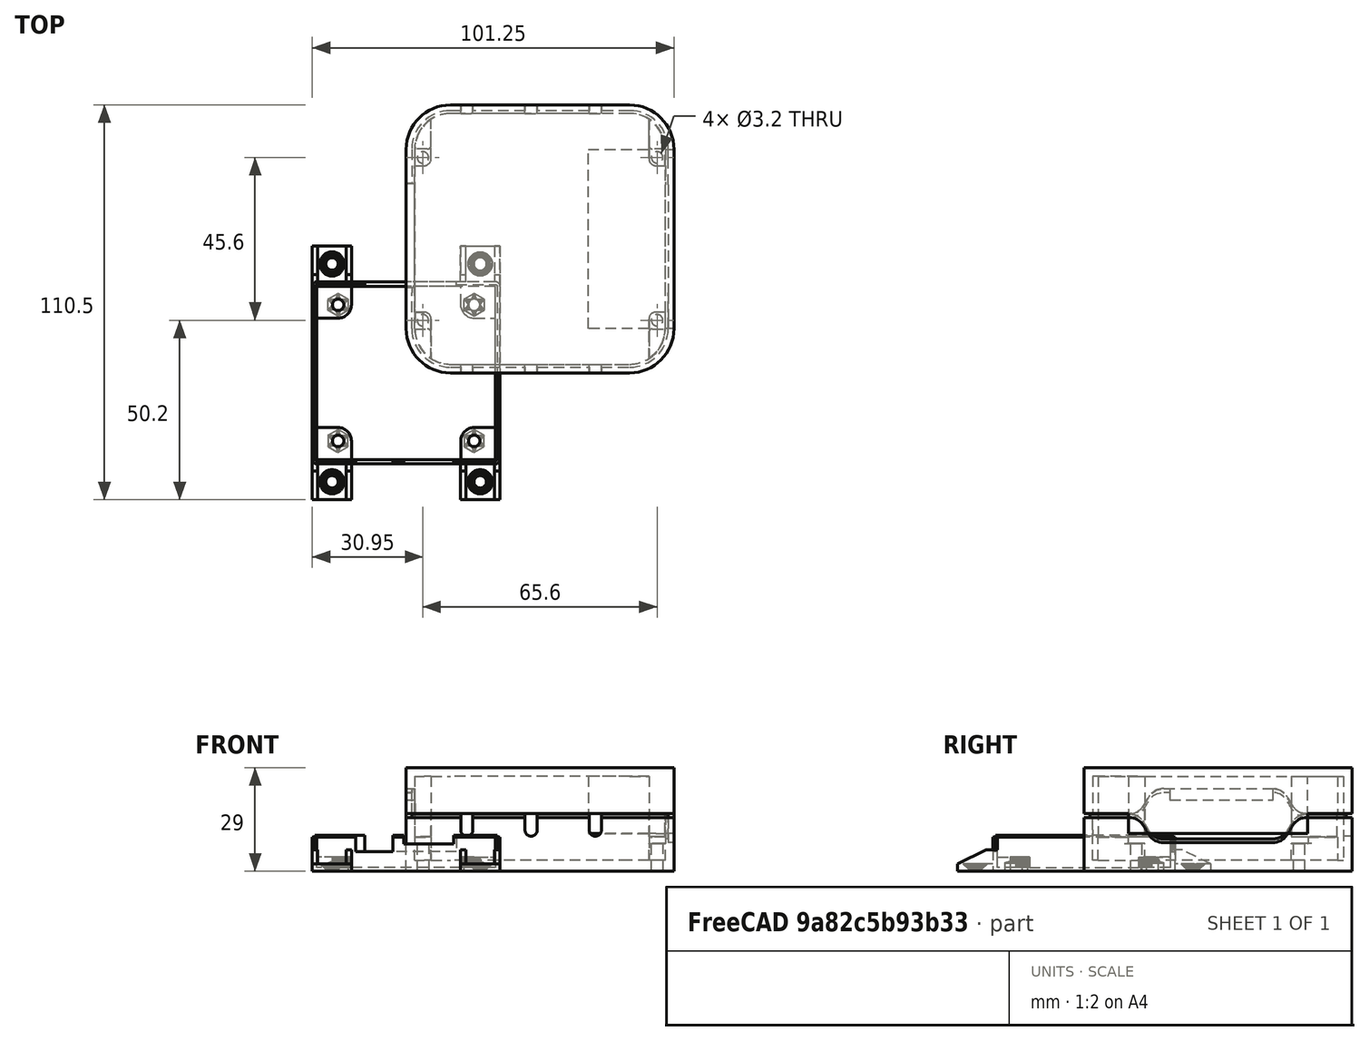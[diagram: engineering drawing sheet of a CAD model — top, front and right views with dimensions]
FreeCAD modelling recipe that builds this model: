
FCSTD DOCUMENT  (FreeCAD 1.0R39109 (Git))
Label: peepSensorCenter
License: All rights reserved
LicenseURL: https://en.wikipedia.org/wiki/All_rights_reserved
objects: Sketcher::SketchObject×20, PartDesign::Pocket×11, PartDesign::Pad×9, PartDesign::Fillet×5, Part::Feature×2, PartDesign::Body×2, Mesh::Feature×1, Part::Refine×1, PartDesign::Thickness×1
note: 123 computed .brp shape members not serialized (recipe doc carries the construction recipe); baked Part::Feature solids carry a one-line shape summary decoded from their .brp

FEATURE [Sketcher::SketchObject] Sketch  label="BaseBrickSketch"
  ArcFitTolerance = 1e-06
  AttachmentSupport = -> [XY_Plane]
  FullyConstrained = true
  MakeInternals = false
  MapMode = 5
  sketch-geometry (4):
    g0: LineSegment StartX=0 StartY=0 StartZ=0 EndX=75 EndY=0 EndZ=0
    g1: LineSegment StartX=75 StartY=0 StartZ=0 EndX=75 EndY=75 EndZ=0
    g2: LineSegment StartX=75 StartY=75 StartZ=0 EndX=0 EndY=75 EndZ=0
    g3: LineSegment StartX=0 StartY=75 StartZ=0 EndX=0 EndY=0 EndZ=0
  constraints (11):
    c: Coincident(g0,g1)
    c: Coincident(g1,g2)
    c: Coincident(g2,g3)
    c: Coincident(g3,g0)
    c: Horizontal(g0)
    c: Horizontal(g2)
    c: Vertical(g1)
    c: Vertical(g3)
    c: Coincident(g0,g-1)
    c: DistanceY(g3,g3) = 75
    c: DistanceX(g2,g2) = 75
FEATURE [PartDesign::Pad] Pad  label="BaseBrick"
  Direction = (0,0,1)
  Length = 15
  Length2 = 10
  Profile = -> Sketch
  ReferenceAxis = -> Sketch [N_Axis]
  Refine = true
  Suppressed = false
  Type = 0
FEATURE [Sketcher::SketchObject] Sketch001  label="BrickHoleSketch"
  ArcFitTolerance = 1e-06
  AttachmentSupport = -> [Pad]
  ExternalGeometry = -> [Pad]
  FullyConstrained = true
  MakeInternals = false
  MapMode = 5
  Placement = pos=(0,0,15) rot=(0,0,1;0rad)
  sketch-geometry (4):
    g0: LineSegment StartX=2.4 StartY=72.6 StartZ=0 EndX=2.4 EndY=2.4 EndZ=0
    g1: LineSegment StartX=2.4 StartY=2.4 StartZ=0 EndX=72.6 EndY=2.4 EndZ=0
    g2: LineSegment StartX=72.6 StartY=2.4 StartZ=0 EndX=72.6 EndY=72.6 EndZ=0
    g3: LineSegment StartX=72.6 StartY=72.6 StartZ=0 EndX=2.4 EndY=72.6 EndZ=0
  constraints (12):
    c: Coincident(g0,g1)
    c: Coincident(g1,g2)
    c: Coincident(g2,g3)
    c: Coincident(g3,g0)
    c: Vertical(g0)
    c: Vertical(g2)
    c: Horizontal(g1)
    c: Horizontal(g3)
    c: DistanceY(g0,g-4) = 2.4
    c: DistanceX(g-4,g0) = 2.4
    c: DistanceY(g-6,g1) = 2.4
    c: DistanceX(g1,g-6) = 2.4
FEATURE [PartDesign::Pocket] Pocket  label="BrickHole"
  BaseFeature = -> Pad
  Direction = (0,0,-1)
  Length = 12
  Length2 = 5
  Profile = -> Sketch001
  ReferenceAxis = -> Sketch001 [N_Axis]
  Refine = true
  Suppressed = false
  Type = 0
  expr: Length = 15 - 3
FEATURE [Sketcher::SketchObject] Sketch002  label="PCBBaseSketch"
  ArcFitTolerance = 1e-06
  AttachmentSupport = -> [Pocket]
  ExternalGeometry = -> [Pocket]
  FullyConstrained = true
  MakeInternals = false
  MapMode = 5
  Placement = pos=(0,0,3) rot=(0,0,1;0rad)
  sketch-geometry (21):
    g0: LineSegment [constr] StartX=2.4 StartY=62.6 StartZ=0 EndX=2.4 EndY=12.4 EndZ=0
    g1: LineSegment [constr] StartX=2.4 StartY=12.4 StartZ=0 EndX=72.6 EndY=12.4 EndZ=0
    g2: LineSegment [constr] StartX=72.6 StartY=12.4 StartZ=0 EndX=72.6 EndY=62.6 EndZ=0
    g3: LineSegment [constr] StartX=72.6 StartY=62.6 StartZ=0 EndX=2.4 EndY=62.6 EndZ=0
    g4: GeomPoint X=2.4 Y=37.5 Z=0
    g5: LineSegment StartX=2.4 StartY=62.6 StartZ=0 EndX=2.4 EndY=58 EndZ=0
    g6: LineSegment StartX=2.4 StartY=58 StartZ=0 EndX=7 EndY=58 EndZ=0
    g7: LineSegment StartX=7 StartY=58 StartZ=0 EndX=7 EndY=62.6 EndZ=0
    g8: LineSegment StartX=7 StartY=62.6 StartZ=0 EndX=2.4 EndY=62.6 EndZ=0
    g9: LineSegment StartX=72.6 StartY=62.6 StartZ=0 EndX=68 EndY=62.6 EndZ=0
    g10: LineSegment StartX=68 StartY=62.6 StartZ=0 EndX=68 EndY=58 EndZ=0
    g11: LineSegment StartX=68 StartY=58 StartZ=0 EndX=72.6 EndY=58 EndZ=0
    g12: LineSegment StartX=72.6 StartY=58 StartZ=0 EndX=72.6 EndY=62.6 EndZ=0
    g13: LineSegment StartX=72.6 StartY=12.4 StartZ=0 EndX=72.6 EndY=17 EndZ=0
    g14: LineSegment StartX=72.6 StartY=17 StartZ=0 EndX=68 EndY=17 EndZ=0
    g15: LineSegment StartX=68 StartY=17 StartZ=0 EndX=68 EndY=12.4 EndZ=0
    g16: LineSegment StartX=68 StartY=12.4 StartZ=0 EndX=72.6 EndY=12.4 EndZ=0
    g17: LineSegment StartX=2.4 StartY=12.4 StartZ=0 EndX=7 EndY=12.4 EndZ=0
    g18: LineSegment StartX=7 StartY=12.4 StartZ=0 EndX=7 EndY=17 EndZ=0
    g19: LineSegment StartX=7 StartY=17 StartZ=0 EndX=2.4 EndY=17 EndZ=0
    g20: LineSegment StartX=2.4 StartY=17 StartZ=0 EndX=2.4 EndY=12.4 EndZ=0
  constraints (56):
    c: Coincident(g0,g1)
    c: Coincident(g1,g2)
    c: Coincident(g2,g3)
    c: Coincident(g3,g0)
    c: Vertical(g0)
    c: Vertical(g2)
    c: Horizontal(g1)
    c: Horizontal(g3)
    c: Symmetric(g-3,g-3,g4)
    c: Symmetric(g0,g0,g4)
    c: Coincident(g5,g6)
    c: Coincident(g6,g7)
    c: Coincident(g7,g8)
    c: Coincident(g8,g5)
    c: Vertical(g5)
    c: Vertical(g7)
    c: Horizontal(g6)
    c: Horizontal(g8)
    c: Coincident(g5,g0)
    c: Coincident(g9,g10)
    c: Coincident(g10,g11)
    c: Coincident(g11,g12)
    c: Coincident(g12,g9)
    c: Horizontal(g9)
    c: Horizontal(g11)
    c: Vertical(g10)
    c: Vertical(g12)
    c: Coincident(g9,g2)
    c: Coincident(g13,g14)
    c: Coincident(g14,g15)
    c: Coincident(g15,g16)
    c: Coincident(g16,g13)
    c: Vertical(g13)
    c: Vertical(g15)
    c: Horizontal(g14)
    c: Horizontal(g16)
    c: Coincident(g13,g1)
    c: Coincident(g17,g18)
    c: Coincident(g18,g19)
    c: Coincident(g19,g20)
    c: Coincident(g20,g17)
    c: Horizontal(g17)
    c: Horizontal(g19)
    c: Vertical(g18)
    c: Vertical(g20)
    c: Coincident(g17,g0)
    c: DistanceX(g19,g19) = 4.6
    c: DistanceX(g6,g6) = 4.6
    c: DistanceX(g11,g11) = 4.6
    c: DistanceX(g14,g14) = 4.6
    c: DistanceY(g15,g15) = 4.6
    c: DistanceY(g10,g10) = 4.6
    c: DistanceY(g7,g7) = 4.6
    c: DistanceY(g18,g18) = 4.6
    c: PointOnObject(g1,g-7)
    c: DistanceY(g1,g2) = 50.2
FEATURE [PartDesign::Pad] Pad001  label="PCBBase"
  BaseFeature = -> Pocket
  Direction = (0,0,1)
  Length = 4.8
  Length2 = 10
  Profile = -> Sketch002
  ReferenceAxis = -> Sketch002 [N_Axis]
  Refine = true
  Suppressed = false
  Type = 0
FEATURE [Mesh::Feature] bottom
FEATURE [Part::Feature] bottom001
  shape: bbox 52.5 x 71 x 10 mm, 3748 faces, 0 solids (baked)
FEATURE [Part::Feature] bottom001_solid  label="bottom001 (Solid)"
  shape: bbox 52.5 x 71 x 10 mm, 3748 faces (baked)
FEATURE [Part::Refine] bottom001_solid001  label="bottom001 (Solid)001"
  Source = -> bottom001_solid
FEATURE [Sketcher::SketchObject] Sketch003  label="ScrewHoleSketch"
  ArcFitTolerance = 1e-06
  AttachmentSupport = -> [Pad001]
  ExternalGeometry = -> [Pad001]
  FullyConstrained = true
  MakeInternals = false
  MapMode = 5
  Placement = pos=(0,0,7.8) rot=(0,0,1;0rad)
  sketch-geometry (20):
    g0: LineSegment [constr] StartX=7 StartY=60.3 StartZ=0 EndX=4.7 EndY=60.3 EndZ=0
    g1: LineSegment [constr] StartX=4.7 StartY=60.3 StartZ=0 EndX=4.7 EndY=58 EndZ=0
    g2: LineSegment [constr] StartX=4.7 StartY=58 StartZ=0 EndX=7 EndY=58 EndZ=0
    g3: LineSegment [constr] StartX=7 StartY=58 StartZ=0 EndX=7 EndY=60.3 EndZ=0
    g4: LineSegment [constr] StartX=4.7 StartY=17 StartZ=0 EndX=4.7 EndY=14.7 EndZ=0
    g5: LineSegment [constr] StartX=4.7 StartY=14.7 StartZ=0 EndX=7 EndY=14.7 EndZ=0
    g6: LineSegment [constr] StartX=7 StartY=14.7 StartZ=0 EndX=7 EndY=17 EndZ=0
    g7: LineSegment [constr] StartX=7 StartY=17 StartZ=0 EndX=4.7 EndY=17 EndZ=0
    g8: LineSegment [constr] StartX=70.3 StartY=17 StartZ=0 EndX=68 EndY=17 EndZ=0
    g9: LineSegment [constr] StartX=68 StartY=17 StartZ=0 EndX=68 EndY=14.7 EndZ=0
    g10: LineSegment [constr] StartX=68 StartY=14.7 StartZ=0 EndX=70.3 EndY=14.7 EndZ=0
    g11: LineSegment [constr] StartX=70.3 StartY=14.7 StartZ=0 EndX=70.3 EndY=17 EndZ=0
    g12: LineSegment [constr] StartX=68 StartY=60.3 StartZ=0 EndX=68 EndY=58 EndZ=0
    g13: LineSegment [constr] StartX=68 StartY=58 StartZ=0 EndX=70.3 EndY=58 EndZ=0
    g14: LineSegment [constr] StartX=70.3 StartY=58 StartZ=0 EndX=70.3 EndY=60.3 EndZ=0
    g15: LineSegment [constr] StartX=70.3 StartY=60.3 StartZ=0 EndX=68 EndY=60.3 EndZ=0
    g16: Circle CenterX=4.7 CenterY=60.3 CenterZ=0 NormalX=0 NormalY=0 NormalZ=1 AngleXU=0 Radius=1.6
    g17: Circle CenterX=4.7 CenterY=14.7 CenterZ=0 NormalX=0 NormalY=0 NormalZ=1 AngleXU=0 Radius=1.6
    g18: Circle CenterX=70.3 CenterY=14.7 CenterZ=0 NormalX=0 NormalY=0 NormalZ=1 AngleXU=0 Radius=1.6
    g19: Circle CenterX=70.3 CenterY=60.3 CenterZ=0 NormalX=0 NormalY=0 NormalZ=1 AngleXU=0 Radius=1.6
  constraints (48):
    c: Coincident(g0,g1)
    c: Coincident(g1,g2)
    c: Coincident(g2,g3)
    c: Coincident(g3,g0)
    c: Horizontal(g0)
    c: Horizontal(g2)
    c: Vertical(g1)
    c: Vertical(g3)
    c: Symmetric(g-3,g-3,g0)
    c: Symmetric(g-4,g-4,g1)
    c: Coincident(g4,g5)
    c: Coincident(g5,g6)
    c: Coincident(g6,g7)
    c: Coincident(g7,g4)
    c: Vertical(g4)
    c: Vertical(g6)
    c: Horizontal(g5)
    c: Horizontal(g7)
    c: Symmetric(g-5,g-5,g4)
    c: Symmetric(g-6,g-6,g5)
    c: Coincident(g8,g9)
    c: Coincident(g9,g10)
    c: Coincident(g10,g11)
    c: Coincident(g11,g8)
    c: Horizontal(g8)
    c: Horizontal(g10)
    c: Vertical(g9)
    c: Vertical(g11)
    c: Symmetric(g-8,g-8,g8)
    c: Symmetric(g-7,g-7,g9)
    c: Coincident(g12,g13)
    c: Coincident(g13,g14)
    c: Coincident(g14,g15)
    c: Coincident(g15,g12)
    c: Vertical(g12)
    c: Vertical(g14)
    c: Horizontal(g13)
    c: Horizontal(g15)
    c: Symmetric(g-9,g-9,g12)
    c: Symmetric(g-10,g-10,g13)
    c: Coincident(g16,g0)
    c: Coincident(g17,g4)
    c: Coincident(g18,g10)
    c: Coincident(g19,g14)
    c: Diameter(g19) = 3.2
    c: Diameter(g18) = 3.2
    c: Diameter(g17) = 3.2
    c: Diameter(g16) = 3.2
FEATURE [PartDesign::Pocket] Pocket001  label="ScrewHole"
  BaseFeature = -> Pad001
  Direction = (0,0,-1)
  Length = 5
  Length2 = 5
  Profile = -> Sketch003
  ReferenceAxis = -> Sketch003 [N_Axis]
  Refine = true
  Suppressed = false
  Type = 1
FEATURE [Sketcher::SketchObject] Sketch004  label="PCBStopSketch"
  ArcFitTolerance = 1e-06
  AttachmentSupport = -> [Pocket001]
  ExternalGeometry = -> [Pocket001]
  FullyConstrained = true
  MakeInternals = false
  MapMode = 5
  Placement = pos=(0,0,3) rot=(0,0,1;0rad)
  sketch-geometry (16):
    g0: LineSegment StartX=68 StartY=12.4 StartZ=0 EndX=68 EndY=2.4 EndZ=0
    g1: LineSegment StartX=68 StartY=2.4 StartZ=0 EndX=72.6 EndY=2.4 EndZ=0
    g2: LineSegment StartX=72.6 StartY=2.4 StartZ=0 EndX=72.6 EndY=12.4 EndZ=0
    g3: LineSegment StartX=72.6 StartY=12.4 StartZ=0 EndX=68 EndY=12.4 EndZ=0
    g4: LineSegment StartX=68 StartY=62.6 StartZ=0 EndX=72.6 EndY=62.6 EndZ=0
    g5: LineSegment StartX=72.6 StartY=62.6 StartZ=0 EndX=72.6 EndY=72.6 EndZ=0
    g6: LineSegment StartX=72.6 StartY=72.6 StartZ=0 EndX=68 EndY=72.6 EndZ=0
    g7: LineSegment StartX=68 StartY=72.6 StartZ=0 EndX=68 EndY=62.6 EndZ=0
    g8: LineSegment StartX=7 StartY=62.6 StartZ=0 EndX=7 EndY=72.6 EndZ=0
    g9: LineSegment StartX=7 StartY=72.6 StartZ=0 EndX=2.4 EndY=72.6 EndZ=0
    g10: LineSegment StartX=2.4 StartY=72.6 StartZ=0 EndX=2.4 EndY=62.6 EndZ=0
    g11: LineSegment StartX=2.4 StartY=62.6 StartZ=0 EndX=7 EndY=62.6 EndZ=0
    g12: LineSegment StartX=7 StartY=12.4 StartZ=0 EndX=2.4 EndY=12.4 EndZ=0
    g13: LineSegment StartX=2.4 StartY=12.4 StartZ=0 EndX=2.4 EndY=2.4 EndZ=0
    g14: LineSegment StartX=2.4 StartY=2.4 StartZ=0 EndX=7 EndY=2.4 EndZ=0
    g15: LineSegment StartX=7 StartY=2.4 StartZ=0 EndX=7 EndY=12.4 EndZ=0
  constraints (40):
    c: Coincident(g0,g1)
    c: Coincident(g1,g2)
    c: Coincident(g2,g3)
    c: Coincident(g3,g0)
    c: Vertical(g0)
    c: Vertical(g2)
    c: Horizontal(g1)
    c: Horizontal(g3)
    c: Coincident(g0,g-11)
    c: Coincident(g1,g-12)
    c: Coincident(g4,g5)
    c: Coincident(g5,g6)
    c: Coincident(g6,g7)
    c: Coincident(g7,g4)
    c: Horizontal(g4)
    c: Horizontal(g6)
    c: Vertical(g5)
    c: Vertical(g7)
    c: Coincident(g4,g-6)
    c: Coincident(g5,g-7)
    c: Coincident(g8,g9)
    c: Coincident(g9,g10)
    c: Coincident(g10,g11)
    c: Coincident(g11,g8)
    c: Vertical(g8)
    c: Vertical(g10)
    c: Horizontal(g9)
    c: Horizontal(g11)
    c: Coincident(g8,g-5)
    c: Coincident(g9,g-4)
    c: Coincident(g12,g13)
    c: Coincident(g13,g14)
    c: Coincident(g14,g15)
    c: Coincident(g15,g12)
    c: Horizontal(g12)
    c: Horizontal(g14)
    c: Vertical(g13)
    c: Vertical(g15)
    c: Coincident(g12,g-10)
    c: Coincident(g13,g-9)
FEATURE [PartDesign::Pad] Pad002  label="PCBStop"
  BaseFeature = -> Pocket001
  Direction = (0,0,1)
  Length = 6.5
  Length2 = 10
  Profile = -> Sketch004
  ReferenceAxis = -> Sketch004 [N_Axis]
  Refine = true
  Suppressed = false
  Type = 0
FEATURE [PartDesign::Fillet] Fillet  label="InnerFillet"
  Base = -> Pad002 [Edge39,Edge46,Edge40,Edge29]
  BaseFeature = -> Pad002
  Radius = 10
  Refine = true
  SupportTransform = false
  Suppressed = false
  UseAllEdges = false
FEATURE [PartDesign::Fillet] Fillet001  label="OuterFillet"
  Base = -> Fillet [Edge50,Edge52,Edge49,Edge54]
  BaseFeature = -> Fillet
  Radius = 12.4
  Refine = true
  SupportTransform = false
  Suppressed = false
  UseAllEdges = false
FEATURE [Sketcher::SketchObject] Sketch005  label="InterlaceWallSketch"
  ArcFitTolerance = 1e-06
  AttachmentSupport = -> [Fillet001]
  ExternalGeometry = -> [Fillet001]
  FullyConstrained = true
  MakeInternals = false
  MapMode = 5
  Placement = pos=(0,0,15) rot=(0,0,1;0rad)
  sketch-geometry (20):
    g0: LineSegment StartX=1.6 StartY=62.6 StartZ=0 EndX=1.6 EndY=12.4 EndZ=0
    g1: LineSegment StartX=12.4 StartY=1.6 StartZ=0 EndX=62.6 EndY=1.6 EndZ=0
    g2: LineSegment StartX=73.4 StartY=12.4 StartZ=0 EndX=73.4 EndY=62.6 EndZ=0
    g3: LineSegment StartX=62.6 StartY=73.4 StartZ=0 EndX=12.4 EndY=73.4 EndZ=0
    g4: ArcOfCircle CenterX=12.4 CenterY=62.6 CenterZ=0 NormalX=0 NormalY=0 NormalZ=1 AngleXU=0 Radius=10.8 StartAngle=1.5708 EndAngle=3.14159
    g5: ArcOfCircle CenterX=12.4 CenterY=12.4 CenterZ=0 NormalX=0 NormalY=0 NormalZ=1 AngleXU=0 Radius=10.8 StartAngle=3.14159 EndAngle=4.71239
    g6: ArcOfCircle CenterX=62.6 CenterY=12.4 CenterZ=0 NormalX=0 NormalY=0 NormalZ=1 AngleXU=0 Radius=10.8 StartAngle=4.71239 EndAngle=6.28319
    g7: ArcOfCircle CenterX=62.6 CenterY=62.6 CenterZ=0 NormalX=0 NormalY=0 NormalZ=1 AngleXU=0 Radius=10.8 StartAngle=0 EndAngle=1.5708
    g8: GeomPoint [constr] X=1.6 Y=73.4 Z=0
    g9: GeomPoint [constr] X=73.4 Y=1.6 Z=0
    g10: LineSegment StartX=2.4 StartY=62.6 StartZ=0 EndX=2.4 EndY=12.4 EndZ=0
    g11: LineSegment StartX=12.4 StartY=2.4 StartZ=0 EndX=62.6 EndY=2.4 EndZ=0
    g12: LineSegment StartX=72.6 StartY=12.4 StartZ=0 EndX=72.6 EndY=62.6 EndZ=0
    g13: LineSegment StartX=62.6 StartY=72.6 StartZ=0 EndX=12.4 EndY=72.6 EndZ=0
    g14: ArcOfCircle CenterX=12.4 CenterY=62.6 CenterZ=0 NormalX=0 NormalY=0 NormalZ=1 AngleXU=0 Radius=10 StartAngle=1.5708 EndAngle=3.14159
    g15: ArcOfCircle CenterX=12.4 CenterY=12.4 CenterZ=0 NormalX=0 NormalY=0 NormalZ=1 AngleXU=0 Radius=10 StartAngle=3.14159 EndAngle=4.71239
    g16: ArcOfCircle CenterX=62.6 CenterY=12.4 CenterZ=0 NormalX=0 NormalY=0 NormalZ=1 AngleXU=0 Radius=10 StartAngle=4.71239 EndAngle=6.28319
    g17: ArcOfCircle CenterX=62.6 CenterY=62.6 CenterZ=0 NormalX=0 NormalY=0 NormalZ=1 AngleXU=0 Radius=10 StartAngle=1e-16 EndAngle=1.5708
    g18: GeomPoint [constr] X=2.4 Y=72.6 Z=0
    g19: GeomPoint [constr] X=72.6 Y=2.4 Z=0
  constraints (45):
    c: Tangent(g0,g4) = -1.5708
    c: Tangent(g0,g5) = -1.5708
    c: Tangent(g1,g5) = -1.5708
    c: Tangent(g1,g6) = -1.5708
    c: Tangent(g2,g6) = -1.5708
    c: Tangent(g2,g7) = -1.5708
    c: Tangent(g3,g7) = -1.5708
    c: Tangent(g3,g4) = -1.5708
    c: Vertical(g0)
    c: Vertical(g2)
    c: Horizontal(g1)
    c: Horizontal(g3)
    c: Equal(g4,g5)
    c: Equal(g5,g6)
    c: Equal(g6,g7)
    c: PointOnObject(g8,g0)
    c: PointOnObject(g8,g3)
    c: PointOnObject(g9,g1)
    c: PointOnObject(g9,g2)
    c: Vertical(g3,g-3)
    c: Horizontal(g0,g-4)
    c: Horizontal(g2,g-5)
    c: DistanceX(g0,g-4) = 0.8
    c: Vertical(g1,g-6)
    c: Tangent(g10,g14) = -1.5708
    c: Tangent(g10,g15) = -1.5708
    c: Tangent(g11,g15) = -1.5708
    c: Tangent(g11,g16) = -1.5708
    c: Tangent(g12,g16) = -1.5708
    c: Tangent(g12,g17) = -1.5708
    c: Tangent(g13,g17) = -1.5708
    c: Tangent(g13,g14) = -1.5708
    c: Vertical(g10)
    c: Vertical(g12)
    c: Horizontal(g13)
    c: Equal(g14,g15)
    c: Equal(g15,g16)
    c: Equal(g16,g17)
    c: PointOnObject(g18,g10)
    c: PointOnObject(g18,g13)
    c: PointOnObject(g19,g11)
    c: PointOnObject(g19,g12)
    c: Coincident(g12,g-5)
    c: Coincident(g11,g-6)
    c: Coincident(g10,g-4)
FEATURE [PartDesign::Pad] Pad003  label="InterlaceWall"
  BaseFeature = -> Fillet001
  Direction = (0,0,1)
  Length = 1
  Length2 = 10
  Profile = -> Sketch005
  ReferenceAxis = -> Sketch005 [N_Axis]
  Refine = true
  Suppressed = false
  Type = 0
FEATURE [Sketcher::SketchObject] Sketch006  label="WireHolesSketch"
  ArcFitTolerance = 1e-06
  AttachmentSupport = -> [XZ_Plane]
  ExternalGeometry = -> [Pad003]
  FullyConstrained = true
  MakeInternals = false
  MapMode = 5
  Placement = pos=(0,0,0) rot=(1,0,0;1.5708rad)
  sketch-geometry (13):
    g0: ArcOfCircle CenterX=17 CenterY=16 CenterZ=0 NormalX=0 NormalY=0 NormalZ=1 AngleXU=0 Radius=1.7 StartAngle=9e-16 EndAngle=3.14159
    g1: ArcOfCircle CenterX=17 CenterY=11.5 CenterZ=0 NormalX=0 NormalY=0 NormalZ=1 AngleXU=0 Radius=1.7 StartAngle=3.14159 EndAngle=6.28319
    g2: LineSegment StartX=18.7 StartY=16 StartZ=0 EndX=18.7 EndY=11.5 EndZ=0
    g3: LineSegment StartX=15.3 StartY=16 StartZ=0 EndX=15.3 EndY=11.5 EndZ=0
    g4: GeomPoint [constr] X=7 Y=11.5 Z=0
    g5: ArcOfCircle CenterX=35 CenterY=16 CenterZ=0 NormalX=0 NormalY=0 NormalZ=1 AngleXU=0 Radius=1.7 StartAngle=3.74e-14 EndAngle=3.14159
    g6: ArcOfCircle CenterX=35 CenterY=11.5 CenterZ=0 NormalX=0 NormalY=0 NormalZ=1 AngleXU=0 Radius=1.7 StartAngle=3.14159 EndAngle=6.28319
    g7: LineSegment StartX=36.7 StartY=16 StartZ=0 EndX=36.7 EndY=11.5 EndZ=0
    g8: LineSegment StartX=33.3 StartY=16 StartZ=0 EndX=33.3 EndY=11.5 EndZ=0
    g9: ArcOfCircle CenterX=53 CenterY=16 CenterZ=0 NormalX=0 NormalY=0 NormalZ=1 AngleXU=0 Radius=1.7 StartAngle=4e-16 EndAngle=3.14159
    g10: ArcOfCircle CenterX=53 CenterY=11.5 CenterZ=0 NormalX=0 NormalY=0 NormalZ=1 AngleXU=0 Radius=1.7 StartAngle=3.14159 EndAngle=6.28319
    g11: LineSegment StartX=54.7 StartY=16 StartZ=0 EndX=54.7 EndY=11.5 EndZ=0
    g12: LineSegment StartX=51.3 StartY=16 StartZ=0 EndX=51.3 EndY=11.5 EndZ=0
  constraints (32):
    c: Tangent(g0,g2) = 1.5708
    c: Tangent(g0,g3) = -1.5708
    c: Tangent(g1,g2) = 1.5708
    c: Tangent(g1,g3) = -1.5708
    c: Equal(g0,g1)
    c: PointOnObject(g0,g-3)
    c: Vertical(g2)
    c: DistanceX(g1,g1) = 3.4
    c: DistanceY(g-5,g4) = 2
    c: Horizontal(g4,g1)
    c: Vertical(g-5,g4)
    c: DistanceX(g4,g1) = 10
    c: Tangent(g5,g7) = 1.5708
    c: Tangent(g5,g8) = -1.5708
    c: Tangent(g6,g7) = 1.5708
    c: Tangent(g6,g8) = -1.5708
    c: Equal(g5,g6)
    c: Vertical(g8)
    c: PointOnObject(g5,g-3)
    c: Tangent(g9,g11) = 1.5708
    c: Tangent(g9,g12) = -1.5708
    c: Tangent(g10,g11) = 1.5708
    c: Tangent(g10,g12) = -1.5708
    c: Equal(g9,g10)
    c: PointOnObject(g9,g-3)
    c: Vertical(g11)
    c: Horizontal(g1,g6)
    c: Horizontal(g6,g10)
    c: DistanceX(g1,g6) = 18
    c: DistanceX(g6,g10) = 18
    c: DistanceX(g6,g6) = 3.4
    c: DistanceX(g10,g10) = 3.4
FEATURE [PartDesign::Pocket] Pocket002  label="WireHoles"
  BaseFeature = -> Pad003
  Direction = (0,1,-2e-16)
  Length = 5
  Length2 = 5
  Profile = -> Sketch006
  ReferenceAxis = -> Sketch006 [N_Axis]
  Refine = true
  Suppressed = false
  Type = 1
FEATURE [Sketcher::SketchObject] Sketch007  label="ChargingPanelLowerSketch"
  ArcFitTolerance = 1e-06
  AttachmentSupport = -> [YZ_Plane]
  ExternalGeometry = -> [Pocket002]
  FullyConstrained = true
  MakeInternals = false
  MapMode = 5
  Placement = pos=(0,0,0) rot=(0.57735,0.57735,0.57735;2.0944rad)
  sketch-geometry (20):
    g0-g4: Circle [constr] x5 (B-spline internal-alignment scaffolding for g5; pole/knot coordinates omitted)
    g5: BSplineCurve PolesCount=5 KnotsCount=3 Degree=3 IsPeriodic=0
    g6: GeomPoint [constr] X=62.6 Y=15 Z=0
    g7: GeomPoint [constr] X=57.6 Y=18.5 Z=0
    g8: GeomPoint [constr] X=52.6 Y=22 Z=0
    g9-g13: Circle [constr] x5 (B-spline internal-alignment scaffolding for g14; pole/knot coordinates omitted)
    g14: BSplineCurve PolesCount=5 KnotsCount=3 Degree=3 IsPeriodic=0
    g15: GeomPoint [constr] X=12.4 Y=15 Z=0
    g16: GeomPoint [constr] X=17.4 Y=18.5 Z=0
    g17: GeomPoint [constr] X=22.4 Y=22 Z=0
    g18: LineSegment StartX=52.6 StartY=22 StartZ=0 EndX=22.4 EndY=22 EndZ=0
    g19: LineSegment StartX=62.6 StartY=15 StartZ=0 EndX=12.4 EndY=15 EndZ=0
  constraints (32):
    c: Weight(g0) = 1
    c: Equal(g0, g1-g4) x4
    c: InternalAlignment(g0-g4 -> g5) x5
    c: InternalAlignment(g6,g5)
    c: InternalAlignment(g7,g5)
    c: InternalAlignment(g8,g5)
    c: Coincident(g0,g-3)
    c: PointOnObject(g1,g-3)
    c: Weight(g9) = 1
    c: Equal(g9, g10-g13) x4
    c: InternalAlignment(g9-g13 -> g14) x5
    c: InternalAlignment(g15,g14)
    c: InternalAlignment(g16,g14)
    c: InternalAlignment(g17,g14)
    c: Coincident(g9,g-3)
    c: PointOnObject(g10,g-3)
    c: DistanceX(g1,g5) = 3
    c: DistanceX(g2,g1) = 2
    c: Coincident(g2,g7)
    c: DistanceX(g5,g3) = 3
    c: Horizontal(g3,g5)
    c: DistanceY(g5,g5) = 7
    c: Coincident(g18,g5)
    c: Coincident(g18,g14)
    c: Coincident(g19,g5)
    c: Coincident(g19,g14)
    c: Horizontal(g18)
    c: Horizontal(g12,g14)
    c: Coincident(g11,g16)
    c: DistanceX(g12,g14) = 3
    c: DistanceX(g11,g12) = 2
    c: DistanceX(g9,g10) = 3
FEATURE [PartDesign::Pad] Pad004  label="ChargingPanelLower"
  BaseFeature = -> Pocket002
  Direction = (1,0,0)
  Length = 1.6
  Length2 = 10
  Profile = -> Sketch007
  ReferenceAxis = -> Sketch007 [N_Axis]
  Refine = true
  Suppressed = false
  Type = 0
FEATURE [PartDesign::Fillet] Fillet002  label="PCBBaseFillet"
  Base = -> Pad004 [Edge243,Edge249,Edge256,Edge247]
  BaseFeature = -> Pad004
  Radius = 2
  Refine = true
  SupportTransform = false
  Suppressed = false
  UseAllEdges = false
FEATURE [Sketcher::SketchObject] Sketch008  label="PCBStopToleranceSketch"
  ArcFitTolerance = 1e-06
  AttachmentSupport = -> [Fillet002]
  ExternalGeometry = -> [Fillet002]
  FullyConstrained = true
  MakeInternals = false
  MapMode = 5
  Placement = pos=(0,0,9.5) rot=(0,0,1;0rad)
  sketch-geometry (16):
    g0: LineSegment StartX=7 StartY=62.6 StartZ=0 EndX=7 EndY=62.7 EndZ=0
    g1: LineSegment StartX=7 StartY=62.7 StartZ=0 EndX=2.4 EndY=62.7 EndZ=0
    g2: LineSegment StartX=2.4 StartY=62.7 StartZ=0 EndX=2.4 EndY=62.6 EndZ=0
    g3: LineSegment StartX=2.4 StartY=62.6 StartZ=0 EndX=7 EndY=62.6 EndZ=0
    g4: LineSegment StartX=72.6 StartY=62.6 StartZ=0 EndX=72.6 EndY=62.7 EndZ=0
    g5: LineSegment StartX=72.6 StartY=62.7 StartZ=0 EndX=68 EndY=62.7 EndZ=0
    g6: LineSegment StartX=68 StartY=62.7 StartZ=0 EndX=68 EndY=62.6 EndZ=0
    g7: LineSegment StartX=68 StartY=62.6 StartZ=0 EndX=72.6 EndY=62.6 EndZ=0
    g8: LineSegment StartX=72.6 StartY=12.4 StartZ=0 EndX=68 EndY=12.4 EndZ=0
    g9: LineSegment StartX=68 StartY=12.4 StartZ=0 EndX=68 EndY=12.3 EndZ=0
    g10: LineSegment StartX=68 StartY=12.3 StartZ=0 EndX=72.6 EndY=12.3 EndZ=0
    g11: LineSegment StartX=72.6 StartY=12.3 StartZ=0 EndX=72.6 EndY=12.4 EndZ=0
    g12: LineSegment StartX=7 StartY=12.4 StartZ=0 EndX=2.4 EndY=12.4 EndZ=0
    g13: LineSegment StartX=2.4 StartY=12.4 StartZ=0 EndX=2.4 EndY=12.3 EndZ=0
    g14: LineSegment StartX=2.4 StartY=12.3 StartZ=0 EndX=7 EndY=12.3 EndZ=0
    g15: LineSegment StartX=7 StartY=12.3 StartZ=0 EndX=7 EndY=12.4 EndZ=0
  constraints (40):
    c: Coincident(g0,g1)
    c: Coincident(g1,g2)
    c: Coincident(g2,g3)
    c: Coincident(g3,g0)
    c: Vertical(g0)
    c: Vertical(g2)
    c: Horizontal(g1)
    c: Coincident(g0,g-3)
    c: Coincident(g4,g5)
    c: Coincident(g5,g6)
    c: Coincident(g6,g7)
    c: Coincident(g7,g4)
    c: Vertical(g4)
    c: Vertical(g6)
    c: Horizontal(g5)
    c: Coincident(g4,g-4)
    c: Coincident(g8,g9)
    c: Coincident(g9,g10)
    c: Coincident(g10,g11)
    c: Coincident(g11,g8)
    c: Horizontal(g10)
    c: Vertical(g9)
    c: Vertical(g11)
    c: Coincident(g8,g-5)
    c: Coincident(g12,g13)
    c: Coincident(g13,g14)
    c: Coincident(g14,g15)
    c: Coincident(g15,g12)
    c: Horizontal(g14)
    c: Vertical(g13)
    c: Vertical(g15)
    c: Coincident(g12,g-6)
    c: Coincident(g12,g-6)
    c: Coincident(g2,g-3)
    c: Coincident(g6,g-4)
    c: Coincident(g8,g-5)
    c: DistanceY(g9,g9) = 0.1
    c: DistanceY(g15,g15) = 0.1
    c: DistanceY(g0,g0) = 0.1
    c: DistanceY(g6,g6) = 0.1
FEATURE [PartDesign::Pocket] Pocket003  label="PCBStopTolerance"
  BaseFeature = -> Fillet002
  Direction = (0,0,-1)
  Length = 1.7
  Length2 = 5
  Profile = -> Sketch008
  ReferenceAxis = -> Sketch008 [N_Axis]
  Refine = true
  Suppressed = false
  Type = 0
  UpToShape = -> [Fillet002]
FEATURE [PartDesign::Fillet] Fillet003  label="PCBStopFillet"
  Base = -> Pocket003 [Edge23,Edge66,Edge101,Edge59]
  BaseFeature = -> Pocket003
  Radius = 1
  Refine = true
  SupportTransform = false
  Suppressed = false
  UseAllEdges = false
FEATURE [Sketcher::SketchObject] Sketch009  label="ButtonPocketHigherSketch"
  ArcFitTolerance = 1e-06
  AttachmentSupport = -> [Fillet003]
  ExternalGeometry = -> [Fillet003]
  FullyConstrained = true
  MakeInternals = false
  MapMode = 5
  Placement = pos=(75,0,0) rot=(0.57735,0.57735,0.57735;2.0944rad)
  sketch-geometry (20):
    g0-g4: Circle [constr] x5 (B-spline internal-alignment scaffolding for g5; pole/knot coordinates omitted)
    g5: BSplineCurve PolesCount=5 KnotsCount=3 Degree=3 IsPeriodic=0
    g6: GeomPoint [constr] X=12.4 Y=16 Z=0
    g7: GeomPoint [constr] X=17.4 Y=12.5 Z=0
    g8: GeomPoint [constr] X=22.4 Y=9 Z=0
    g9: LineSegment StartX=12.4 StartY=16 StartZ=0 EndX=62.6 EndY=16 EndZ=0
    g10: LineSegment StartX=22.4 StartY=9 StartZ=0 EndX=52.6 EndY=9 EndZ=0
    g11-g15: Circle [constr] x5 (B-spline internal-alignment scaffolding for g16; pole/knot coordinates omitted)
    g16: BSplineCurve PolesCount=5 KnotsCount=3 Degree=3 IsPeriodic=0
    g17: GeomPoint [constr] X=62.6 Y=16 Z=0
    g18: GeomPoint [constr] X=57.6 Y=12.5 Z=0
    g19: GeomPoint [constr] X=52.6 Y=9 Z=0
  constraints (32):
    c: Weight(g0) = 1
    c: Equal(g0, g1-g4) x4
    c: InternalAlignment(g0-g4 -> g5) x5
    c: InternalAlignment(g6,g5)
    c: InternalAlignment(g7,g5)
    c: InternalAlignment(g8,g5)
    c: Distance(g0,g1) = 3
    c: Coincident(g0,g-3)
    c: PointOnObject(g1,g-3)
    c: Coincident(g2,g7)
    c: Horizontal(g3,g5)
    c: DistanceX(g3,g5) = 3
    c: DistanceX(g2,g3) = 2
    c: Coincident(g9,g5)
    c: Coincident(g9,g-3)
    c: Coincident(g10,g5)
    c: Horizontal(g10)
    c: DistanceY(g5,g0) = 7
    c: Weight(g11) = 1
    c: Equal(g11, g12-g15) x4
    c: InternalAlignment(g11-g15 -> g16) x5
    c: InternalAlignment(g17,g16)
    c: InternalAlignment(g18,g16)
    c: InternalAlignment(g19,g16)
    c: Distance(g11,g12) = 3
    c: Coincident(g11,g9)
    c: PointOnObject(g12,g9)
    c: Coincident(g15,g10)
    c: DistanceX(g16,g14) = 3
    c: Coincident(g18,g13)
    c: DistanceX(g14,g13) = 2
    c: Horizontal(g14,g16)
FEATURE [PartDesign::Pocket] Pocket004  label="ButtonPocketHigher"
  BaseFeature = -> Fillet003
  Direction = (-1,0,0)
  Length = 2.4
  Length2 = 5
  Profile = -> Sketch009
  ReferenceAxis = -> Sketch009 [N_Axis]
  Refine = true
  Suppressed = false
  Type = 0
FEATURE [Sketcher::SketchObject] Sketch010  label="ButtonPocketLowerSketch"
  ArcFitTolerance = 1e-06
  AttachmentSupport = -> [Pocket004]
  ExternalGeometry = -> [Pocket004]
  FullyConstrained = true
  MakeInternals = false
  MapMode = 5
  Placement = pos=(75,0,0) rot=(0.57735,0.57735,0.57735;2.0944rad)
  sketch-geometry (22):
    g0: LineSegment StartX=12.4 StartY=16 StartZ=0 EndX=62.6 EndY=16 EndZ=0
    g1: LineSegment StartX=62.6 StartY=16 StartZ=0 EndX=62.6 EndY=15 EndZ=0
    g2: LineSegment StartX=12.4 StartY=16 StartZ=0 EndX=12.4 EndY=15 EndZ=0
    g3: LineSegment StartX=22.4 StartY=8 StartZ=0 EndX=52.6 EndY=8 EndZ=0
    g4-g8: Circle [constr] x5 (B-spline internal-alignment scaffolding for g9; pole/knot coordinates omitted)
    g9: BSplineCurve PolesCount=5 KnotsCount=3 Degree=3 IsPeriodic=0
    g10: GeomPoint [constr] X=12.4 Y=15 Z=0
    g11: GeomPoint [constr] X=17.4 Y=11.5 Z=0
    g12: GeomPoint [constr] X=22.4 Y=8 Z=0
    g13-g17: Circle [constr] x5 (B-spline internal-alignment scaffolding for g18; pole/knot coordinates omitted)
    g18: BSplineCurve PolesCount=5 KnotsCount=3 Degree=3 IsPeriodic=0
    g19: GeomPoint [constr] X=52.6 Y=8 Z=0
    g20: GeomPoint [constr] X=57.6 Y=11.5 Z=0
    g21: GeomPoint [constr] X=62.6 Y=15 Z=0
  constraints (36):
    c: Coincident(g0,g-3)
    c: Coincident(g0,g-4)
    c: Coincident(g1,g0)
    c: Coincident(g1,g-4)
    c: Coincident(g2,g0)
    c: Coincident(g2,g-3)
    c: Horizontal(g3)
    c: Weight(g4) = 1
    c: Equal(g4, g5-g8) x4
    c: InternalAlignment(g4-g8 -> g9) x5
    c: InternalAlignment(g10,g9)
    c: InternalAlignment(g11,g9)
    c: InternalAlignment(g12,g9)
    c: Coincident(g4,g2)
    c: Coincident(g8,g3)
    c: Weight(g13) = 1
    c: Equal(g13, g14-g17) x4
    c: InternalAlignment(g13-g17 -> g18) x5
    c: InternalAlignment(g19,g18)
    c: InternalAlignment(g20,g18)
    c: InternalAlignment(g21,g18)
    c: Coincident(g13,g3)
    c: Coincident(g17,g1)
    c: Horizontal(g18,g14)
    c: Horizontal(g16,g18)
    c: Coincident(g15,g20)
    c: DistanceX(g16,g18) = 3
    c: DistanceX(g15,g16) = 2
    c: DistanceX(g18,g14) = 3
    c: DistanceY(g18,g18) = 7
    c: Horizontal(g7,g9)
    c: Horizontal(g9,g5)
    c: Coincident(g6,g11)
    c: DistanceX(g7,g9) = 3
    c: DistanceX(g9,g5) = 3
    c: DistanceX(g5,g6) = 2
FEATURE [PartDesign::Pocket] Pocket005  label="ButtonPocketLower"
  BaseFeature = -> Pocket004
  Direction = (-1,0,0)
  Length = 1.6
  Length2 = 5
  Profile = -> Sketch010
  ReferenceAxis = -> Sketch010 [N_Axis]
  Refine = true
  Suppressed = false
  Type = 0
FEATURE [Sketcher::SketchObject] Sketch011  label="ChargingPanelHigherSketch"
  ArcFitTolerance = 1e-06
  AttachmentSupport = -> [Pocket005]
  ExternalGeometry = -> [Pocket005]
  FullyConstrained = true
  MakeInternals = false
  MapMode = 5
  Placement = pos=(2.4,0,-9e-16) rot=(0.57735,0.57735,0.57735;2.0944rad)
  sketch-geometry (20):
    g0-g4: Circle [constr] x5 (B-spline internal-alignment scaffolding for g5; pole/knot coordinates omitted)
    g5: BSplineCurve PolesCount=5 KnotsCount=3 Degree=3 IsPeriodic=0
    g6: GeomPoint [constr] X=12.4 Y=16 Z=0
    g7: GeomPoint [constr] X=17.4 Y=19.5 Z=0
    g8: GeomPoint [constr] X=22.4 Y=23 Z=0
    g9-g13: Circle [constr] x5 (B-spline internal-alignment scaffolding for g14; pole/knot coordinates omitted)
    g14: BSplineCurve PolesCount=5 KnotsCount=3 Degree=3 IsPeriodic=0
    g15: GeomPoint [constr] X=62.6 Y=16 Z=0
    g16: GeomPoint [constr] X=57.6 Y=19.5 Z=0
    g17: GeomPoint [constr] X=52.6 Y=23 Z=0
    g18: LineSegment StartX=12.4 StartY=16 StartZ=0 EndX=62.6 EndY=16 EndZ=0
    g19: LineSegment StartX=52.6 StartY=23 StartZ=0 EndX=22.4 EndY=23 EndZ=0
  constraints (32):
    c: Weight(g0) = 1
    c: Equal(g0, g1-g4) x4
    c: InternalAlignment(g0-g4 -> g5) x5
    c: InternalAlignment(g6,g5)
    c: InternalAlignment(g7,g5)
    c: InternalAlignment(g8,g5)
    c: Coincident(g0,g-3)
    c: PointOnObject(g1,g-3)
    c: Weight(g9) = 1
    c: Equal(g9, g10-g13) x4
    c: InternalAlignment(g9-g13 -> g14) x5
    c: InternalAlignment(g15,g14)
    c: InternalAlignment(g16,g14)
    c: InternalAlignment(g17,g14)
    c: Coincident(g9,g-3)
    c: PointOnObject(g10,g-3)
    c: Coincident(g18,g5)
    c: Coincident(g18,g14)
    c: Coincident(g19,g14)
    c: Coincident(g19,g5)
    c: Horizontal(g19)
    c: Coincident(g7,g2)
    c: Horizontal(g3,g5)
    c: Horizontal(g14,g12)
    c: Coincident(g11,g16)
    c: DistanceX(g3,g5) = 3
    c: DistanceX(g2,g3) = 2
    c: DistanceY(g0,g5) = 7
    c: DistanceX(g0,g1) = 3
    c: DistanceX(g14,g12) = 3
    c: DistanceX(g12,g11) = 2
    c: DistanceX(g10,g9) = 3
FEATURE [PartDesign::Pad] Pad005  label="ChargingPanelHigher"
  BaseFeature = -> Pocket005
  Direction = (1,0,0)
  Length = 0.8
  Length2 = 10
  Profile = -> Sketch011
  ReferenceAxis = -> Sketch011 [N_Axis]
  Refine = true
  Reversed = true
  Suppressed = false
  Type = 0
FEATURE [Sketcher::SketchObject] Sketch012  label="ChargerPocketSketch"
  ArcFitTolerance = 1e-06
  AttachmentSupport = -> [YZ_Plane]
  ExternalGeometry = -> [Pad005]
  FullyConstrained = true
  MakeInternals = false
  MapMode = 5
  Placement = pos=(0,0,0) rot=(0.57735,0.57735,0.57735;2.0944rad)
  sketch-geometry (4):
    g0: LineSegment StartX=53 StartY=23 StartZ=0 EndX=24 EndY=23 EndZ=0
    g1: LineSegment StartX=24 StartY=23 StartZ=0 EndX=24 EndY=20 EndZ=0
    g2: LineSegment StartX=24 StartY=20 StartZ=0 EndX=53 EndY=20 EndZ=0
    g3: LineSegment StartX=53 StartY=20 StartZ=0 EndX=53 EndY=23 EndZ=0
  constraints (12):
    c: Coincident(g0,g1)
    c: Coincident(g1,g2)
    c: Coincident(g2,g3)
    c: Coincident(g3,g0)
    c: Horizontal(g0)
    c: Horizontal(g2)
    c: Vertical(g1)
    c: Vertical(g3)
    c: PointOnObject(g0,g-4)
    c: DistanceX(g2,g-3) = 22
    c: DistanceY(g1,g1) = 3
    c: DistanceX(g-1,g1) = 24
FEATURE [PartDesign::Pocket] Pocket006  label="ChargerPocket"
  BaseFeature = -> Pad005
  Direction = (-1,0,0)
  Length = 2.4
  Length2 = 5
  Profile = -> Sketch012
  ReferenceAxis = -> Sketch012 [N_Axis]
  Refine = true
  Reversed = true
  Suppressed = false
  Type = 0
FEATURE [PartDesign::Body] Body  label="Base"
  AllowCompound = false
  Group = -> [Sketch,Pad,Sketch001,Pocket,Sketch002,Pad001,Sketch003,Pocket001,Sketch004,Pad002,Fillet,Fillet001,Sketch005,Pad003,Sketch006,Pocket002,Sketch007,Pad004,Fillet002,Sketch008,Pocket003,Fillet003,Sketch009,Pocket004,Sketch010,Pocket005,Sketch011,Pad005,Sketch012,Pocket006]
  Origin = -> Origin
  Tip = -> Pocket006
FEATURE [Sketcher::SketchObject] Sketch013  label="CoverBrickSketch"
  ArcFitTolerance = 1e-06
  AttachmentSupport = -> [XY_Plane001]
  FullyConstrained = true
  MakeInternals = false
  MapMode = 5
  sketch-geometry (10):
    g0: LineSegment StartX=12.4 StartY=0 StartZ=0 EndX=62.6 EndY=0 EndZ=0
    g1: LineSegment StartX=75 StartY=12.4 StartZ=0 EndX=75 EndY=62.6 EndZ=0
    g2: LineSegment StartX=62.6 StartY=75 StartZ=0 EndX=12.4 EndY=75 EndZ=0
    g3: LineSegment StartX=0 StartY=62.6 StartZ=0 EndX=0 EndY=12.4 EndZ=0
    g4: ArcOfCircle CenterX=12.4 CenterY=12.4 CenterZ=0 NormalX=0 NormalY=0 NormalZ=1 AngleXU=0 Radius=12.4 StartAngle=3.14159 EndAngle=4.71239
    g5: ArcOfCircle CenterX=62.6 CenterY=12.4 CenterZ=0 NormalX=0 NormalY=0 NormalZ=1 AngleXU=0 Radius=12.4 StartAngle=4.71239 EndAngle=6.28319
    g6: ArcOfCircle CenterX=62.6 CenterY=62.6 CenterZ=0 NormalX=0 NormalY=0 NormalZ=1 AngleXU=0 Radius=12.4 StartAngle=-5.4854e-12 EndAngle=1.5708
    g7: ArcOfCircle CenterX=12.4 CenterY=62.6 CenterZ=0 NormalX=0 NormalY=0 NormalZ=1 AngleXU=0 Radius=12.4 StartAngle=1.5708 EndAngle=3.14159
    g8: GeomPoint [constr] X=0 Y=0 Z=0
    g9: GeomPoint [constr] X=75 Y=75 Z=0
  constraints (23):
    c: Tangent(g0,g4) = -1.5708
    c: Tangent(g0,g5) = -1.5708
    c: Tangent(g1,g5) = -1.5708
    c: Tangent(g1,g6) = -1.5708
    c: Tangent(g2,g6) = -1.5708
    c: Tangent(g2,g7) = -1.5708
    c: Tangent(g3,g7) = -1.5708
    c: Tangent(g3,g4) = -1.5708
    c: Horizontal(g0)
    c: Horizontal(g2)
    c: Vertical(g1)
    c: Vertical(g3)
    c: Equal(g4,g5)
    c: Equal(g5,g6)
    c: Equal(g6,g7)
    c: PointOnObject(g8,g0)
    c: PointOnObject(g8,g3)
    c: PointOnObject(g9,g1)
    c: PointOnObject(g9,g2)
    c: Coincident(g8,g-1)
    c: DistanceY(g0,g2) = 75
    c: DistanceX(g3,g1) = 75
    c: Radius(g6) = 12.4
FEATURE [PartDesign::Pad] Pad006  label="CoverBrick"
  Direction = (0,0,1)
  Length = 12.9
  Length2 = 10
  Profile = -> Sketch013
  ReferenceAxis = -> Sketch013 [N_Axis]
  Refine = true
  Reversed = true
  Suppressed = false
  Type = 0
FEATURE [PartDesign::Thickness] Thickness  label="CoverHole"
  Base = -> Pad006 [Face10]
  BaseFeature = -> Pad006
  Intersection = false
  Join = 0
  Mode = 0
  Refine = true
  Reversed = true
  SupportTransform = false
  Suppressed = false
  Value = 2.4
FEATURE [Sketcher::SketchObject] Sketch014  label="PCBCoverStopSketch"
  ArcFitTolerance = 1e-06
  AttachmentSupport = -> [Thickness]
  ExternalGeometry = -> [Thickness]
  FullyConstrained = true
  MakeInternals = false
  MapMode = 5
  Placement = pos=(0,0,-2.4) rot=(1,0,0;3.14159rad)
  sketch-geometry (20):
    g0: LineSegment StartX=7 StartY=-12.4 StartZ=0 EndX=7 EndY=-3.98335 EndZ=0
    g1: LineSegment StartX=68 StartY=-12.4 StartZ=0 EndX=68 EndY=-3.98335 EndZ=0
    g2: LineSegment StartX=68 StartY=-62.6 StartZ=0 EndX=68 EndY=-71.0167 EndZ=0
    g3: ArcOfCircle CenterX=62.6 CenterY=-62.6 CenterZ=0 NormalX=0 NormalY=0 NormalZ=1 AngleXU=0 Radius=10 StartAngle=5.28283 EndAngle=6.28319
    g4: LineSegment StartX=7 StartY=-62.6 StartZ=0 EndX=7 EndY=-71.0167 EndZ=0
    g5: ArcOfCircle CenterX=12.4 CenterY=-62.6 CenterZ=0 NormalX=0 NormalY=0 NormalZ=1 AngleXU=0 Radius=10 StartAngle=3.14159 EndAngle=4.14195
    g6: LineSegment StartX=2.4 StartY=-17 StartZ=0 EndX=7 EndY=-17 EndZ=0
    g7: LineSegment StartX=7 StartY=-17 StartZ=0 EndX=7 EndY=-12.4 EndZ=0
    g8: LineSegment StartX=2.4 StartY=-12.4 StartZ=0 EndX=2.4 EndY=-17 EndZ=0
    g9: LineSegment StartX=68 StartY=-12.4 StartZ=0 EndX=68 EndY=-17 EndZ=0
    g10: LineSegment StartX=68 StartY=-17 StartZ=0 EndX=72.6 EndY=-17 EndZ=0
    g11: LineSegment StartX=72.6 StartY=-58 StartZ=0 EndX=68 EndY=-58 EndZ=0
    g12: LineSegment StartX=68 StartY=-58 StartZ=0 EndX=68 EndY=-62.6 EndZ=0
    g13: LineSegment StartX=72.6 StartY=-58 StartZ=0 EndX=72.6 EndY=-62.6 EndZ=0
    g14: LineSegment StartX=2.4 StartY=-62.6 StartZ=0 EndX=2.4 EndY=-58 EndZ=0
    g15: LineSegment StartX=2.4 StartY=-58 StartZ=0 EndX=7 EndY=-58 EndZ=0
    g16: LineSegment StartX=7 StartY=-58 StartZ=0 EndX=7 EndY=-62.6 EndZ=0
    g17: ArcOfCircle CenterX=12.4 CenterY=-12.4 CenterZ=0 NormalX=0 NormalY=0 NormalZ=1 AngleXU=0 Radius=10 StartAngle=2.14123 EndAngle=3.14159
    g18: LineSegment StartX=72.6 StartY=-17 StartZ=0 EndX=72.6 EndY=-12.4 EndZ=0
    g19: ArcOfCircle CenterX=62.6 CenterY=-12.4 CenterZ=0 NormalX=0 NormalY=0 NormalZ=1 AngleXU=0 Radius=10 StartAngle=-5.4863e-12 EndAngle=1.00036
  constraints (56):
    c: Vertical(g1)
    c: Vertical(g0)
    c: Vertical(g2)
    c: Coincident(g3,g-8)
    c: Coincident(g3,g2)
    c: Vertical(g4)
    c: Coincident(g5,g-9)
    c: Coincident(g5,g4)
    c: Horizontal(g6)
    c: Coincident(g7,g6)
    c: Vertical(g7)
    c: Coincident(g8,g6)
    c: DistanceY(g7,g7) = 4.6
    c: Coincident(g7,g0)
    c: DistanceX(g6,g6) = 4.6
    c: Coincident(g9,g1)
    c: Vertical(g9)
    c: Coincident(g10,g9)
    c: Horizontal(g10)
    c: DistanceY(g9,g9) = 4.6
    c: Horizontal(g11)
    c: Coincident(g12,g11)
    c: Vertical(g12)
    c: Coincident(g13,g11)
    c: DistanceY(g12,g12) = 4.6
    c: Coincident(g15,g14)
    c: Horizontal(g15)
    c: Coincident(g16,g15)
    c: Vertical(g16)
    c: DistanceY(g16,g16) = 4.6
    c: Vertical(g8)
    c: Horizontal(g8,g0)
    c: Coincident(g17,g-5)
    c: Coincident(g17,g8)
    c: Coincident(g0,g17)
    c: Coincident(g18,g10)
    c: Vertical(g18)
    c: DistanceX(g10,g10) = 4.6
    c: Horizontal(g18,g1)
    c: Coincident(g19,g-7)
    c: Coincident(g19,g18)
    c: Coincident(g19,g1)
    c: Vertical(g13)
    c: Coincident(g12,g2)
    c: Coincident(g13,g3)
    c: Horizontal(g3,g2)
    c: DistanceX(g11,g11) = 4.6
    c: Vertical(g14)
    c: Coincident(g14,g5)
    c: Coincident(g16,g4)
    c: Horizontal(g5,g4)
    c: DistanceX(g15,g15) = 4.6
    c: Coincident(g18,g-7)
    c: Coincident(g3,g-8)
    c: Coincident(g8,g-5)
    c: Coincident(g-9,g5)
FEATURE [PartDesign::Pad] Pad007  label="PCBCoverStop"
  BaseFeature = -> Thickness
  Direction = (0,0,-1)
  Length = 17
  Length2 = 10
  Profile = -> Sketch014
  ReferenceAxis = -> Sketch014 [N_Axis]
  Refine = true
  Suppressed = false
  Type = 0
FEATURE [PartDesign::Fillet] Fillet004  label="PCBCoverStopFillet"
  Base = -> Pad007 [Edge97,Edge100,Edge92,Edge91]
  BaseFeature = -> Pad007
  Radius = 2
  Refine = true
  SupportTransform = false
  Suppressed = false
  UseAllEdges = false
FEATURE [Sketcher::SketchObject] Sketch015
  ArcFitTolerance = 1e-06
  AttachmentSupport = -> [Fillet004]
  ExternalGeometry = -> [Fillet004]
  FullyConstrained = true
  MakeInternals = false
  MapMode = 5
  Placement = pos=(0,0,-19.4) rot=(1,0,0;3.14159rad)
  sketch-geometry (12):
    g0: LineSegment StartX=2.4 StartY=-17 StartZ=0 EndX=2.5 EndY=-17 EndZ=0
    g1: LineSegment StartX=2.5 StartY=-17 StartZ=0 EndX=2.5 EndY=-12.4 EndZ=0
    g2: LineSegment StartX=2.4 StartY=-17 StartZ=0 EndX=2.4 EndY=-12.4 EndZ=0
    g3: LineSegment StartX=7 StartY=-3.98335 StartZ=0 EndX=7 EndY=-4.10241 EndZ=0
    g4: ArcOfCircle CenterX=12.4 CenterY=-12.4 CenterZ=0 NormalX=0 NormalY=0 NormalZ=1 AngleXU=0 Radius=10 StartAngle=2.14123 EndAngle=3.14159
    g5: ArcOfCircle CenterX=12.4 CenterY=-12.4 CenterZ=0 NormalX=0 NormalY=0 NormalZ=1 AngleXU=0 Radius=9.9 StartAngle=2.14773 EndAngle=3.14159
    g6: LineSegment StartX=72.6 StartY=-17 StartZ=0 EndX=72.6 EndY=-12.4 EndZ=0
    g7: LineSegment StartX=72.6 StartY=-17 StartZ=0 EndX=72.5 EndY=-17 EndZ=0
    g8: LineSegment StartX=72.5 StartY=-17 StartZ=0 EndX=72.5 EndY=-12.4 EndZ=0
    g9: LineSegment StartX=68 StartY=-3.98335 StartZ=0 EndX=68 EndY=-4.10241 EndZ=0
    g10: ArcOfCircle CenterX=62.6 CenterY=-12.4 CenterZ=0 NormalX=0 NormalY=0 NormalZ=1 AngleXU=0 Radius=10 StartAngle=-5.4863e-12 EndAngle=1.00036
    g11: ArcOfCircle CenterX=62.6 CenterY=-12.4 CenterZ=0 NormalX=0 NormalY=0 NormalZ=1 AngleXU=0 Radius=9.9 StartAngle=-5.5413e-12 EndAngle=0.993865
  constraints (31):
    c: Coincident(g0,g-4)
    c: PointOnObject(g0,g-4)
    c: Coincident(g1,g0)
    c: Vertical(g1)
    c: Coincident(g2,g0)
    c: Coincident(g2,g-3)
    c: Coincident(g3,g-5)
    c: PointOnObject(g3,g-5)
    c: Horizontal(g1,g2)
    c: Coincident(g4,g-3)
    c: Coincident(g4,g2)
    c: Coincident(g5,g4)
    c: Coincident(g5,g1)
    c: Coincident(g5,g3)
    c: Coincident(g3,g4)
    c: Coincident(g6,g-8)
    c: Coincident(g6,g-7)
    c: Coincident(g7,g6)
    c: PointOnObject(g7,g-8)
    c: Coincident(g8,g7)
    c: Vertical(g8)
    c: Coincident(g9,g-7)
    c: PointOnObject(g9,g-6)
    c: Horizontal(g8,g6)
    c: DistanceX(g7,g7) = 0.1
    c: Coincident(g10,g-7)
    c: Coincident(g10,g9)
    c: Coincident(g10,g6)
    c: Coincident(g11,g10)
    c: Coincident(g11,g9)
    c: Coincident(g11,g8)
FEATURE [PartDesign::Pocket] Pocket007  label="PCBCoverStopTolerance1"
  BaseFeature = -> Fillet004
  Direction = (0,0,1)
  Length = 6.5
  Length2 = 5
  Profile = -> Sketch015
  ReferenceAxis = -> Sketch015 [N_Axis]
  Refine = true
  Suppressed = false
  Type = 0
FEATURE [Sketcher::SketchObject] Sketch016
  ArcFitTolerance = 1e-06
  AttachmentSupport = -> [Pocket007]
  ExternalGeometry = -> [Pocket007]
  FullyConstrained = true
  MakeInternals = false
  MapMode = 5
  Placement = pos=(0,0,-19.4) rot=(1,0,0;3.14159rad)
  sketch-geometry (6):
    g0: LineSegment StartX=72.6 StartY=-58 StartZ=0 EndX=72.6 EndY=-62.6 EndZ=0
    g1: LineSegment StartX=72.6 StartY=-58 StartZ=0 EndX=72.5 EndY=-58 EndZ=0
    g2: LineSegment StartX=72.5 StartY=-58 StartZ=0 EndX=72.5 EndY=-62.6 EndZ=0
    g3: LineSegment StartX=68 StartY=-71.0167 StartZ=0 EndX=68 EndY=-70.8976 EndZ=0
    g4: ArcOfCircle CenterX=62.6 CenterY=-62.6 CenterZ=0 NormalX=0 NormalY=0 NormalZ=1 AngleXU=0 Radius=10 StartAngle=5.28283 EndAngle=6.28319
    g5: ArcOfCircle CenterX=62.6 CenterY=-62.6 CenterZ=0 NormalX=0 NormalY=0 NormalZ=1 AngleXU=0 Radius=9.9 StartAngle=5.28932 EndAngle=6.28319
  constraints (15):
    c: Coincident(g0,g-3)
    c: Coincident(g0,g-4)
    c: Coincident(g1,g0)
    c: PointOnObject(g1,g-3)
    c: Coincident(g2,g1)
    c: Vertical(g2)
    c: Coincident(g3,g-5)
    c: PointOnObject(g3,g-5)
    c: Coincident(g4,g-4)
    c: Coincident(g4,g0)
    c: Coincident(g5,g4)
    c: Coincident(g5,g2)
    c: Coincident(g5,g3)
    c: DistanceX(g1,g1) = 0.1
    c: Coincident(g3,g4)
FEATURE [PartDesign::Pocket] Pocket008  label="PCBCoverStopTolerance2"
  BaseFeature = -> Pocket007
  Direction = (0,0,1)
  Length = 6.5
  Length2 = 5
  Profile = -> Sketch016
  ReferenceAxis = -> Sketch016 [N_Axis]
  Refine = true
  Suppressed = false
  Type = 0
FEATURE [Sketcher::SketchObject] Sketch017
  ArcFitTolerance = 1e-06
  AttachmentSupport = -> [Pocket008]
  ExternalGeometry = -> [Pocket008]
  FullyConstrained = true
  MakeInternals = false
  MapMode = 5
  Placement = pos=(0,0,-19.4) rot=(1,0,0;3.14159rad)
  sketch-geometry (6):
    g0: ArcOfCircle CenterX=12.4 CenterY=-62.6 CenterZ=0 NormalX=0 NormalY=0 NormalZ=1 AngleXU=0 Radius=10 StartAngle=3.14159 EndAngle=4.14195
    g1: LineSegment StartX=2.4 StartY=-58 StartZ=0 EndX=2.5 EndY=-58 EndZ=0
    g2: LineSegment StartX=2.4 StartY=-58 StartZ=0 EndX=2.4 EndY=-62.6 EndZ=0
    g3: LineSegment StartX=2.5 StartY=-58 StartZ=0 EndX=2.5 EndY=-62.6 EndZ=0
    g4: LineSegment StartX=7 StartY=-71.0167 StartZ=0 EndX=7 EndY=-70.8976 EndZ=0
    g5: ArcOfCircle CenterX=12.4 CenterY=-62.6 CenterZ=0 NormalX=0 NormalY=0 NormalZ=1 AngleXU=0 Radius=9.9 StartAngle=3.14159 EndAngle=4.13546
  constraints (16):
    c: Coincident(g0,g-3)
    c: Coincident(g0,g-3)
    c: Horizontal(g0,g0)
    c: Coincident(g1,g-5)
    c: PointOnObject(g1,g-5)
    c: Coincident(g2,g1)
    c: Coincident(g2,g0)
    c: Coincident(g3,g1)
    c: Vertical(g3)
    c: Coincident(g4,g0)
    c: PointOnObject(g4,g-4)
    c: DistanceX(g1,g1) = 0.1
    c: Horizontal(g3,g0)
    c: Coincident(g5,g0)
    c: Coincident(g5,g3)
    c: Coincident(g5,g4)
FEATURE [PartDesign::Pocket] Pocket009  label="PCBCoverStopTolerance3"
  BaseFeature = -> Pocket008
  Direction = (0,0,1)
  Length = 6.5
  Length2 = 5
  Profile = -> Sketch017
  ReferenceAxis = -> Sketch017 [N_Axis]
  Refine = true
  Suppressed = false
  Type = 0
FEATURE [Sketcher::SketchObject] Sketch019
  ArcFitTolerance = 1e-06
  AttachmentSupport = -> [Pocket009]
  ExternalGeometry = -> [Pocket009]
  FullyConstrained = true
  MakeInternals = false
  MapMode = 5
  Placement = pos=(0,0,0) rot=(0.57735,-0.57735,-0.57735;2.0944rad)
  sketch-geometry (20):
    g0-g4: Circle [constr] x5 (B-spline internal-alignment scaffolding for g5; pole/knot coordinates omitted)
    g5: BSplineCurve PolesCount=5 KnotsCount=3 Degree=3 IsPeriodic=0
    g6: GeomPoint [constr] X=-62.6 Y=-12.9 Z=0
    g7: GeomPoint [constr] X=-57.6 Y=-9.4 Z=0
    g8: GeomPoint [constr] X=-52.6 Y=-5.9 Z=0
    g9-g13: Circle [constr] x5 (B-spline internal-alignment scaffolding for g14; pole/knot coordinates omitted)
    g14: BSplineCurve PolesCount=5 KnotsCount=3 Degree=3 IsPeriodic=0
    g15: GeomPoint [constr] X=-12.4 Y=-12.9 Z=0
    g16: GeomPoint [constr] X=-17.4 Y=-9.4 Z=0
    g17: GeomPoint [constr] X=-22.4 Y=-5.9 Z=0
    g18: LineSegment StartX=-62.6 StartY=-12.9 StartZ=0 EndX=-12.4 EndY=-12.9 EndZ=0
    g19: LineSegment StartX=-22.4 StartY=-5.9 StartZ=0 EndX=-52.6 EndY=-5.9 EndZ=0
  constraints (32):
    c: Weight(g0) = 1
    c: Equal(g0, g1-g4) x4
    c: InternalAlignment(g0-g4 -> g5) x5
    c: InternalAlignment(g6,g5)
    c: InternalAlignment(g7,g5)
    c: InternalAlignment(g8,g5)
    c: Coincident(g0,g-3)
    c: PointOnObject(g1,g-3)
    c: Weight(g9) = 1
    c: Equal(g9, g10-g13) x4
    c: InternalAlignment(g9-g13 -> g14) x5
    c: InternalAlignment(g15,g14)
    c: InternalAlignment(g16,g14)
    c: InternalAlignment(g17,g14)
    c: Coincident(g9,g-3)
    c: PointOnObject(g10,g-3)
    c: Coincident(g18,g5)
    c: Coincident(g18,g14)
    c: Coincident(g19,g14)
    c: Coincident(g19,g5)
    c: Horizontal(g19)
    c: Coincident(g2,g7)
    c: Coincident(g11,g16)
    c: DistanceX(g10,g9) = 3
    c: DistanceX(g11,g10) = 2
    c: DistanceX(g14,g12) = 3
    c: Horizontal(g14,g12)
    c: Horizontal(g3,g5)
    c: DistanceX(g3,g5) = 3
    c: DistanceX(g0,g1) = 3
    c: DistanceX(g1,g2) = 2
    c: DistanceY(g0,g5) = 7
FEATURE [PartDesign::Pocket] Pocket010  label="ChargingPanelPocket"
  BaseFeature = -> Pocket009
  Direction = (1,0,0)
  Length = 0
  Length2 = 5
  Profile = -> Sketch019
  ReferenceAxis = -> Sketch019 [N_Axis]
  Refine = true
  Suppressed = false
  Type = 3
  UpToFace = -> Pocket009 [Face33]
FEATURE [Sketcher::SketchObject] Sketch020
  ArcFitTolerance = 1e-06
  AttachmentSupport = -> [Pocket010]
  ExternalGeometry = -> [Pocket010]
  FullyConstrained = true
  MakeInternals = false
  MapMode = 5
  Placement = pos=(0,0,-2.4) rot=(1,0,0;3.14159rad)
  sketch-geometry (4):
    g0: LineSegment StartX=75 StartY=-12.4 StartZ=0 EndX=51 EndY=-12.4 EndZ=0
    g1: LineSegment StartX=51 StartY=-12.4 StartZ=0 EndX=51 EndY=-62.6 EndZ=0
    g2: LineSegment StartX=51 StartY=-62.6 StartZ=0 EndX=75 EndY=-62.6 EndZ=0
    g3: LineSegment StartX=75 StartY=-62.6 StartZ=0 EndX=75 EndY=-12.4 EndZ=0
  constraints (10):
    c: Coincident(g0,g1)
    c: Coincident(g1,g2)
    c: Coincident(g2,g3)
    c: Coincident(g3,g0)
    c: Horizontal(g0)
    c: Horizontal(g2)
    c: Vertical(g1)
    c: Coincident(g0,g-3)
    c: Coincident(g2,g-4)
    c: DistanceX(g2,g2) = 24
FEATURE [PartDesign::Pad] Pad008  label="ButtonContainer"
  BaseFeature = -> Pocket010
  Direction = (0,0,-1)
  Length = 16
  Length2 = 10
  Profile = -> Sketch020
  ReferenceAxis = -> Sketch020 [N_Axis]
  Refine = true
  Suppressed = false
  Type = 0
FEATURE [PartDesign::Body] Body001  label="Cover"
  AllowCompound = false
  Group = -> [Sketch013,Pad006,Thickness,Sketch014,Pad007,Fillet004,Sketch015,Pocket007,Sketch016,Pocket008,Sketch017,Pocket009,Sketch019,Pocket010,Sketch020,Pad008]
  Origin = -> Origin001
  Placement = pos=(0,0,29) rot=(0,0,1;0rad)
  Tip = -> Pad008
